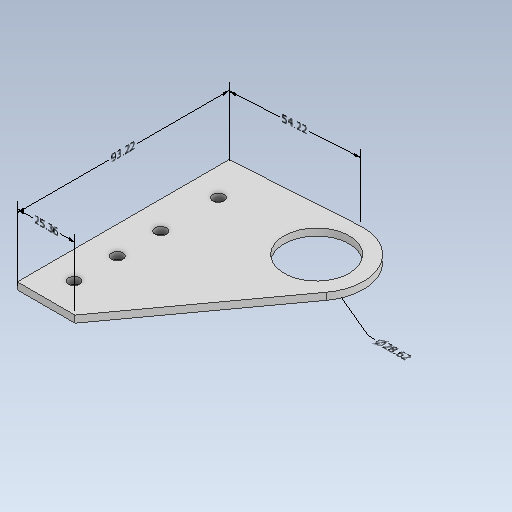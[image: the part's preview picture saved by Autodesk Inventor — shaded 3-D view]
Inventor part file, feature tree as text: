
AUTODESK INVENTOR PART (.ipt)
format: ipt  version: 2023 (Build 270158000, 158)  size: 133,632 bytes
history: native  units: in
note: dims shown in document units (in); Inventor stores cm internally (conversion verified against a paired STEP export)
features: other x5, extrude x1, sketch x1
ambient origin geometry x8: Origin, YZ Plane, XZ Plane, XY Plane, X Axis, Y Axis, Z Axis, Center Point
bodies: Body1 (feature_tree)
feature tree (7):
  other  "Annotations"
  extrude  "Extrusion2"  Depth=0.9984in
  sketch  "Sketch1"  dims[d1=0.9984in d2=3.6701in d3=0.4803in d4=0.4043in d5=0.0984in d10=0.5535in d11=0.0984in d12=0.5535in d13=0.0984in d14=0.8031in d15=0.0984in d16=1.0425in d17=0.562in d25=1.1268in d26=0.2457in d27=0.1209in d28=0.0in d29=2.3953in d30=1.1268in d32=0.0in d33=0.3937in d34=3.6701in d35=0.0in d36=0.3937in d37=2.1346in d38=0.0in d39=0.3937in d40=0.9984in]
  other  "Diameter Dimension 1"
  other  "Linear Dimension 1"
  other  "Linear Dimension 2"
  other  "Linear Dimension 3"
